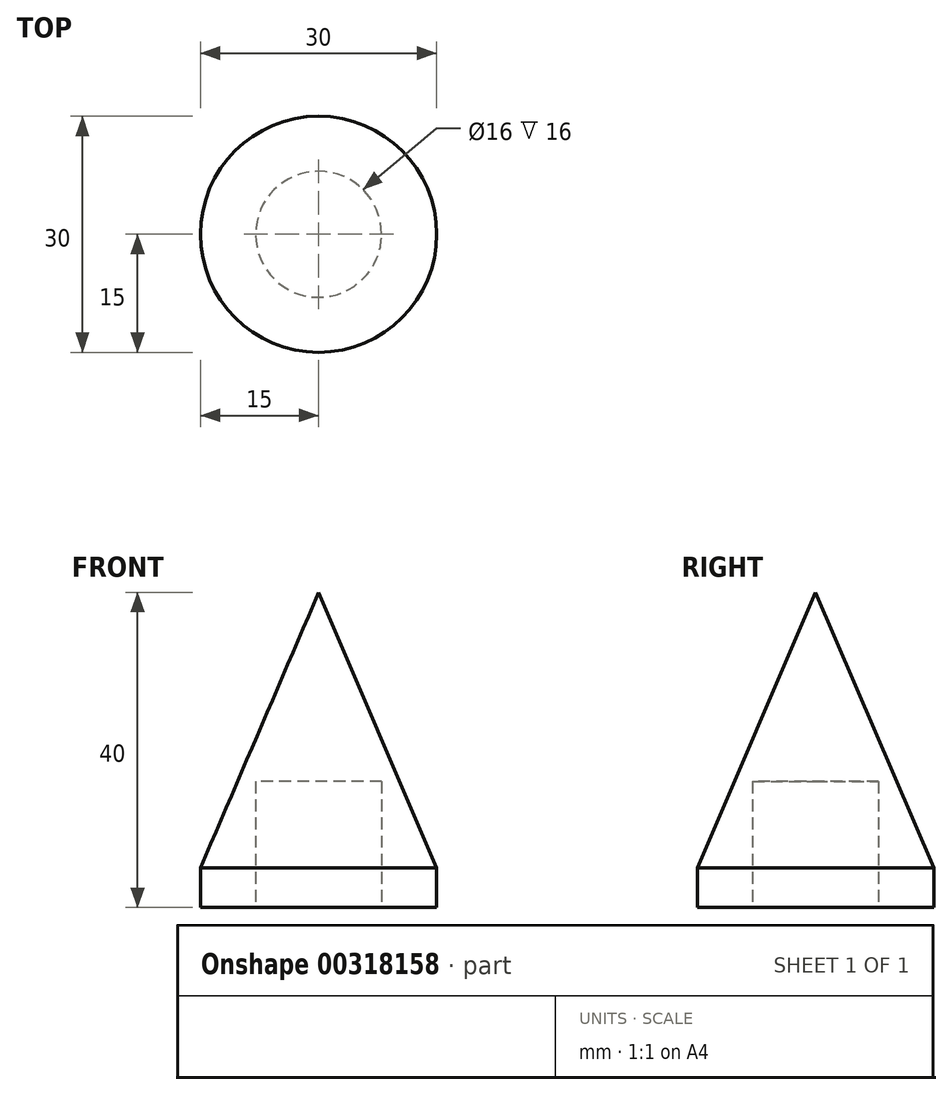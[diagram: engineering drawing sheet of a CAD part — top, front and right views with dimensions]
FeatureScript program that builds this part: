
annotation { "Feature Type Name" : "Feature", "Feature Type Description" : "" }
export const myFeature = defineFeature(function(context is Context, id is Id, definition is map)
    precondition{}
    {
        {
            var Q0;
            Q0=qCreatedBy(makeId("Top.planeOp"),FACE);
            var sketch = newSketch(context, id + "F0", { "sketchPlane" : qUnion([Q0])});
            skCircle(sketch, "E0", {"center": v(0, 0) * mm, "radius": 15 * mm});
            skCircle(sketch, "E1", {"center": v(0, 0) * mm, "radius": 1.5 * mm});
            skCircle(sketch, "E2", {"center": v(0, 0) * mm, "radius": 8 * mm});
            skSolve(sketch);
        }
        {
            var Q0;
            Q0=makeQuery(id+"F0.imprint","IMPRINT",FACE,{"disambiguationData":[TD([[makeQuery(id+"F0.imprint","IMPRINT",EDGE,{"derivedFrom":sQuery(id+"F0.wireOp",EDGE,"E0")}),1.0]])]});
            var Q1;
            Q1=makeQuery(id+"F0.imprint","IMPRINT",FACE,{"disambiguationData":[TD([[makeQuery(id+"F0.imprint","IMPRINT",EDGE,{"derivedFrom":sQuery(id+"F0.wireOp",EDGE,"E1")}),-1.0]])]});
            var Q2;
            Q2=makeQuery(id+"F0.imprint","IMPRINT",FACE,{"disambiguationData":[TD([[makeQuery(id+"F0.imprint","IMPRINT",EDGE,{"derivedFrom":sQuery(id+"F0.wireOp",EDGE,"E1")}),1.0]])]});
            extrude(context, id + "F1", {"entities" : qUnion([Q0, Q1, Q2]), "depth" : 40 * mm});
        }
        {
            var Q0;
            Q0=makeQuery(id+"F0.imprint","IMPRINT",FACE,{"disambiguationData":[TD([[makeQuery(id+"F0.imprint","IMPRINT",EDGE,{"derivedFrom":sQuery(id+"F0.wireOp",EDGE,"E1")}),-1.0]])]});
            var Q1;
            Q1=makeQuery(id+"F0.imprint","IMPRINT",FACE,{"disambiguationData":[TD([[makeQuery(id+"F0.imprint","IMPRINT",EDGE,{"derivedFrom":sQuery(id+"F0.wireOp",EDGE,"E1")}),1.0]])]});
            extrude(context, id + "F2", {"entities" : qUnion([Q0, Q1]), "operationType" : NewBodyOperationType.REMOVE, "depth" : 16 * mm});
        }
        {
            var Q0;
            Q0=makeQuery(id+"F1.opExtrude","CAP_EDGE",EDGE,{"disambiguationData":[OSD([sQuery(id+"F0.wireOp",EDGE,"E0")])],"isStart":false});
            chamfer(context, id + "F3", {"entities" : qUnion([Q0]), "chamferType" : ChamferType.TWO_OFFSETS, "width1" : 15 * mm, "oppositeDirection" : false, "width2" : 35 * mm, "tangentPropagation" : true});
        }
    });
